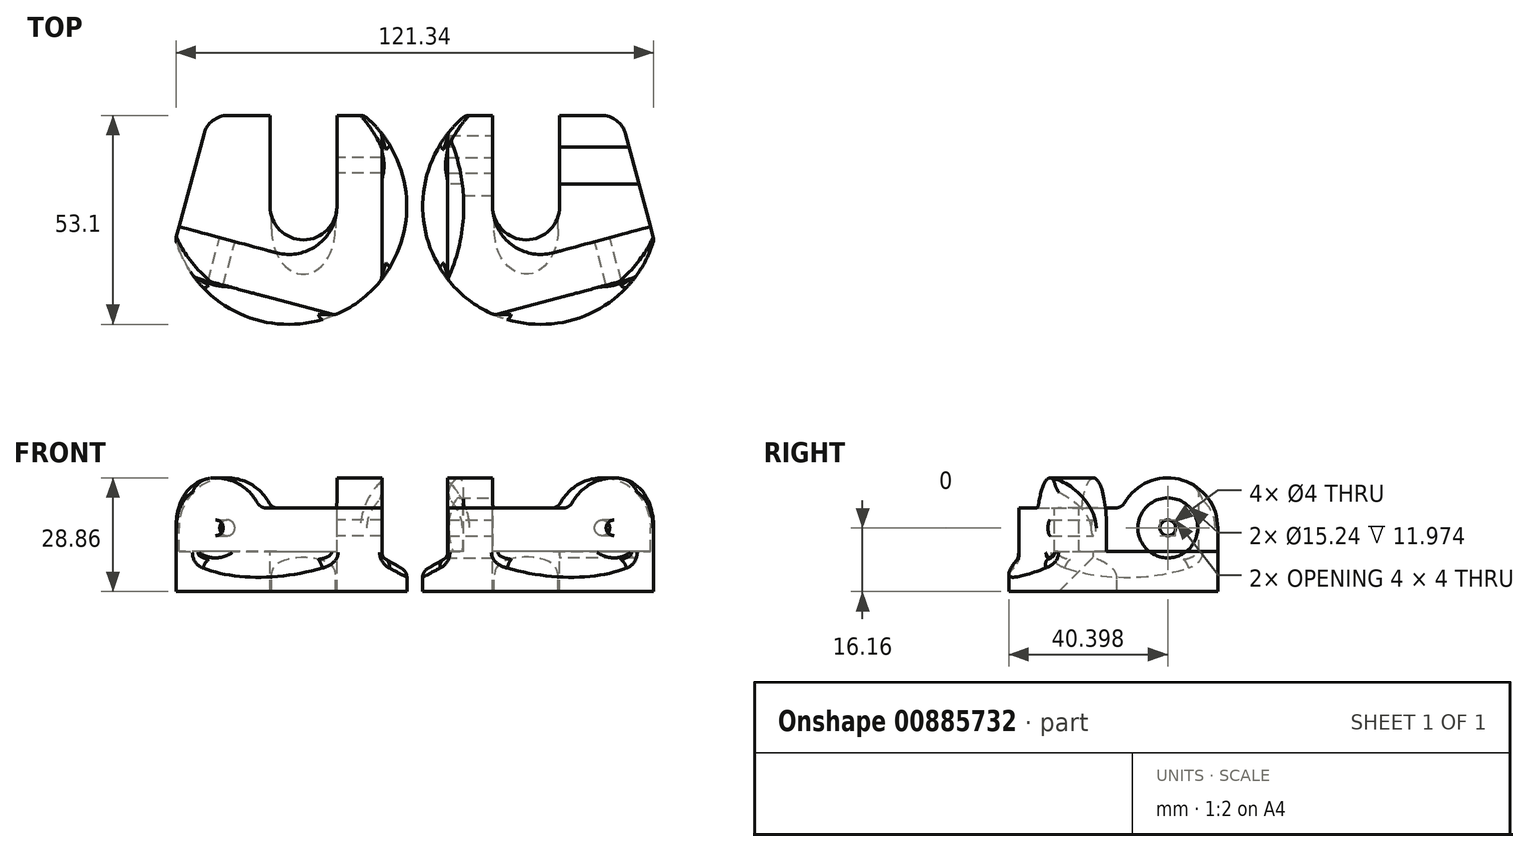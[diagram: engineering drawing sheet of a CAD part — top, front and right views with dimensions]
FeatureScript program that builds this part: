
annotation { "Feature Type Name" : "Feature", "Feature Type Description" : "" }
export const myFeature = defineFeature(function(context is Context, id is Id, definition is map)
    precondition{}
    {
        {
            var Q0;
            Q0=qCreatedBy(makeId("Top.planeOp"),FACE);
            var sketch = newSketch(context, id + "F0", { "sketchPlane" : qUnion([Q0])});
            skCircle(sketch, "E0", {"center": v(-32, 0) * mm, "radius": 30 * mm});
            skSolve(sketch);
        }
        {
            var Q0;
            Q0 = qSketchRegion(id + "F0", true);
            extrude(context, id + "F1", {"entities" : qUnion([Q0]), "depth" : 29 * mm, "offsetDistance" : 25.4 * mm});
        }
        {
            var Q0;
            Q0=makeQuery(id+"F1.opExtrude","CAP_FACE",FACE,{"disambiguationData":[OSD([sQuery(id+"F0.wireOp",EDGE,"E0")])],"isStart":false});
            var sketch = newSketch(context, id + "F2", { "sketchPlane" : qUnion([Q0])});
            skLineSegment(sketch, "E1", {"start": v(-61.63, -4.71) * mm, "end": v(-35.16, -11.8) * mm});
            skLineSegment(sketch, "E2", {"start": v(-19.78, 0) * mm, "end": v(-19.78, 27.4) * mm});
            skLineSegment(sketch, "E3", {"start": v(-8.35, -30.82) * mm, "end": v(-8.35, 27.4) * mm});
            skLineSegment(sketch, "E4", {"start": v(-8.35, -30.82) * mm, "end": v(-64.59, -15.75) * mm});
            skLineSegment(sketch, "E5", {"start": v(-64.59, -15.75) * mm, "end": v(-61.63, -4.71) * mm});
            skLineSegment(sketch, "E6", {"start": v(-19.78, 27.4) * mm, "end": v(-8.35, 27.4) * mm});
            skPoint(sketch, "E7.visualSharp", {"position": v(-19.78, -15.93) * mm});
            skArc(sketch, "E7.filletArc", {"start": v(-35.16, -11.8) * mm, "mid": v(-24.56, -9.7) * mm, "end": v(-19.78, 0) * mm});
            skCircle(sketch, "E8", {"center": v(-32, 0) * mm, "radius": 44.45 * mm});
            skSolve(sketch);
        }
        {
            var Q0;
            Q0 = qSketchRegion(id + "F2", true);
            var Q1;
            Q1=makeQuery(id+"F1.opExtrude","CAP_FACE",FACE,{"disambiguationData":[OSD([sQuery(id+"F0.wireOp",EDGE,"E0")])],"isStart":true});
            extrude(context, id + "F3", {"entities" : qUnion([Q0]), "operationType" : NewBodyOperationType.REMOVE, "endBound" : BoundingType.UP_TO_SURFACE, "oppositeDirection" : true, "depth" : 25.4 * mm, "endBoundEntityFace" : qUnion([Q1]), "hasOffset" : true, "offsetDistance" : 10.16 * mm});
        }
        {
            var Q0;
            {var subQ0=sQuery(id+"F2.wireOp",EDGE,"E1");var subQ1=sQuery(id+"F2.wireOp",EDGE,"E2");var subQ2=sQuery(id+"F2.wireOp",EDGE,"E7.filletArc");Q0=makeQuery(id+"F3.boolean.opBoolean","COPY",FACE,{"disambiguationData":[TD([makeQuery(id+"F3.opExtrude","SWEPT_FACE",FACE,{"disambiguationData":[OSD([subQ0])]})])],"derivedFrom":makeQuery(id+"F3.opExtrude","CAP_FACE",FACE,{"disambiguationData":[OSD([subQ0,subQ1,sQuery(id+"F2.wireOp",EDGE,"E3"),sQuery(id+"F2.wireOp",EDGE,"E4"),sQuery(id+"F2.wireOp",EDGE,"E5"),sQuery(id+"F2.wireOp",EDGE,"E6"),subQ2,sQuery(id+"F2.wireOp",EDGE,"E8")])],"isStart":false})});}
            var sketch = newSketch(context, id + "F4", { "sketchPlane" : qUnion([Q0])});
            skLineSegment(sketch, "E9.bottom", {"start": v(-19.78, 30) * mm, "end": v(-36.8, 30) * mm});
            skLineSegment(sketch, "E9.top", {"start": v(-19.78, 0) * mm, "end": v(-36.8, 0) * mm, "construction": true});
            skLineSegment(sketch, "E9.left", {"start": v(-19.78, 30) * mm, "end": v(-19.78, 0) * mm});
            skLineSegment(sketch, "E9.right", {"start": v(-36.8, 30) * mm, "end": v(-36.8, 0) * mm});
            skArc(sketch, "E10", {"start": v(-36.8, 0) * mm, "mid": v(-28.29, -8.5) * mm, "end": v(-19.78, 0) * mm});
            skSolve(sketch);
        }
        {
            var Q0;
            Q0 = qSketchRegion(id + "F4", true);
            extrude(context, id + "F5", {"entities" : qUnion([Q0]), "operationType" : NewBodyOperationType.REMOVE, "endBound" : BoundingType.THROUGH_ALL, "oppositeDirection" : true, "depth" : 25.4 * mm, "offsetDistance" : 25.4 * mm});
        }
        {
            var Q0;
            Q0=makeQuery(id+"F3.boolean.opBoolean","COPY",FACE,{"derivedFrom":makeQuery(id+"F3.opExtrude","SWEPT_FACE",FACE,{"disambiguationData":[OSD([sQuery(id+"F2.wireOp",EDGE,"E4")])]})});
            var sketch = newSketch(context, id + "F6", { "sketchPlane" : qUnion([Q0])});
            skPoint(sketch, "E11", {"position": v(-43.8, 16.16) * mm});
            skSolve(sketch);
        }
        {
            var Q0;
            Q0=makeQuery(id+"F3.boolean.opBoolean","COPY",FACE,{"derivedFrom":makeQuery(id+"F3.opExtrude","SWEPT_FACE",FACE,{"disambiguationData":[OSD([sQuery(id+"F2.wireOp",EDGE,"E3")])]})});
            var sketch = newSketch(context, id + "F7", { "sketchPlane" : qUnion([Q0])});
            skPoint(sketch, "E12", {"position": v(10.4, 16.16) * mm});
            skSolve(sketch);
        }
        {
            var Q0;
            Q0=sQuery(id+"F7.wireOp",VERTEX,"E12");
            var Q1;
            Q1=sQuery(id+"F6.wireOp",VERTEX,"E11");
            var Q2;
            Q2=makeQuery(id+"F1.opExtrude","SWEPT_BODY",BODY,{"disambiguationData":[OSD([sQuery(id+"F0.wireOp",EDGE,"E0")])]});
            hole(context, id + "F8", {"style" : HoleStyle.SIMPLE, "endStyle" : HoleEndStyle.THROUGH, "holeDiameter" : 4 * mm, "majorDiameter" : 6.35 * mm, "isTappedThrough" : true, "tappedDepth" : 12.7 * mm, "tapClearance" : 3, "locations" : qUnion([Q0, Q1]), "scope" : qUnion([Q2]), "startStyle" : HoleStartStyle.PART});
        }
        {
            var Q0;
            Q0=makeQuery(id+"F3.boolean.opBoolean","COPY",FACE,{"derivedFrom":makeQuery(id+"F3.opExtrude","SWEPT_FACE",FACE,{"disambiguationData":[OSD([sQuery(id+"F2.wireOp",EDGE,"E3")])]})});
            var sketch = newSketch(context, id + "F9", { "sketchPlane" : qUnion([Q0])});
            skCircle(sketch, "E13", {"center": v(10.4, 16.16) * mm, "radius": 7.62 * mm});
            skSolve(sketch);
        }
        {
            var Q0;
            Q0 = qSketchRegion(id + "F9", true);
            extrude(context, id + "F10", {"entities" : qUnion([Q0]), "operationType" : NewBodyOperationType.REMOVE, "endBound" : BoundingType.THROUGH_ALL, "depth" : 25.4 * mm, "offsetDistance" : 25.4 * mm});
        }
        {
            var Q0;
            Q0=makeQuery(id+"F3.boolean.opBoolean","COPY",FACE,{"derivedFrom":makeQuery(id+"F3.opExtrude","SWEPT_FACE",FACE,{"disambiguationData":[OSD([sQuery(id+"F2.wireOp",EDGE,"E4")])]})});
            var sketch = newSketch(context, id + "F11", { "sketchPlane" : qUnion([Q0])});
            skCircle(sketch, "E14", {"center": v(-43.8, 16.16) * mm, "radius": 7.62 * mm});
            skSolve(sketch);
        }
        {
            var Q0;
            Q0 = qSketchRegion(id + "F11", true);
            extrude(context, id + "F12", {"entities" : qUnion([Q0]), "operationType" : NewBodyOperationType.REMOVE, "endBound" : BoundingType.THROUGH_ALL, "depth" : 25.4 * mm, "offsetDistance" : 25.4 * mm});
        }
        {
            var Q0;
            {var subQ0=sQuery(id+"F2.wireOp",EDGE,"E3");Q0=makeQuery(id+"F10.boolean.opBoolean","INTERSECT",EDGE,{"disambiguationData":[OD(1.0)],"derivedFrom":[makeQuery(id+"F3.boolean.opBoolean","COPY",FACE,{"disambiguationData":[TD([makeQuery(id+"F3.opExtrude","SWEPT_FACE",FACE,{"disambiguationData":[OSD([subQ0])]})])],"derivedFrom":makeQuery(id+"F3.opExtrude","CAP_FACE",FACE,{"disambiguationData":[OSD([sQuery(id+"F2.wireOp",EDGE,"E1"),sQuery(id+"F2.wireOp",EDGE,"E2"),subQ0,sQuery(id+"F2.wireOp",EDGE,"E4"),sQuery(id+"F2.wireOp",EDGE,"E5"),sQuery(id+"F2.wireOp",EDGE,"E6"),sQuery(id+"F2.wireOp",EDGE,"E7.filletArc"),sQuery(id+"F2.wireOp",EDGE,"E8")])],"isStart":false})}),makeQuery(id+"F10.opExtrude","SWEPT_FACE",FACE,{"disambiguationData":[OSD([sQuery(id+"F9.wireOp",EDGE,"E13")])]})]});}
            cPlane(context, id + "F13", {"entities" : qUnion([Q0]), "cplaneType" : CPlaneType.LINE_ANGLE, "offset" : 25.4 * mm, "angle" : 45 * degree, "oppositeDirection" : true, "width" : 152.4 * mm, "height" : 152.4 * mm});
        }
        {
            var Q0;
            Q0=qCreatedBy(id+"F13.planeOp",FACE);
            var sketch = newSketch(context, id + "F14", { "sketchPlane" : qUnion([Q0])});
            skLineSegment(sketch, "E15.0", {"start": v(-19.78, 2.07) * mm, "end": v(-19.78, 6.07) * mm, "construction": true});
            skLineSegment(sketch, "E16", {"start": v(-19.78, 4.07) * mm, "end": v(-36.8, 4.07) * mm, "construction": true});
            skLineSegment(sketch, "E17", {"start": v(-36.8, 4.07) * mm, "end": v(-36.8, 0) * mm, "construction": true});
            skArc(sketch, "E18", {"start": v(-20.16, 4.07) * mm, "mid": v(-28.29, 12.2) * mm, "end": v(-36.42, 4.07) * mm});
            skLineSegment(sketch, "E19", {"start": v(-36.42, 4.07) * mm, "end": v(-36.42, 0) * mm});
            skLineSegment(sketch, "E20", {"start": v(-36.42, 0) * mm, "end": v(-20.16, 0) * mm});
            skLineSegment(sketch, "E21", {"start": v(-20.16, 0) * mm, "end": v(-20.16, 4.07) * mm});
            skSolve(sketch);
        }
        {
            var Q0;
            Q0=makeQuery(id+"F14.imprint","IMPRINT",FACE,{"disambiguationData":[TD([[makeQuery(id+"F14.imprint","IMPRINT",EDGE,{"derivedFrom":sQuery(id+"F14.wireOp",EDGE,"E18")}),1.0]])]});
            extrude(context, id + "F15", {"entities" : qUnion([Q0]), "operationType" : NewBodyOperationType.REMOVE, "endBound" : BoundingType.THROUGH_ALL, "depth" : 25.4 * mm, "offsetDistance" : 25.4 * mm});
        }
        {
            var Q0;
            Q0=makeQuery(id+"F10.boolean.opBoolean","MERGE",FACE,{"derivedFrom":[makeQuery(id+"F3.boolean.opBoolean","COPY",FACE,{"derivedFrom":makeQuery(id+"F3.opExtrude","SWEPT_FACE",FACE,{"disambiguationData":[OSD([sQuery(id+"F2.wireOp",EDGE,"E3")])]})})],"fromTools":[makeQuery(id+"F10.opExtrude","CAP_FACE",FACE,{"disambiguationData":[OSD([sQuery(id+"F9.wireOp",EDGE,"E13")])],"isStart":true})]});
            var sketch = newSketch(context, id + "F16", { "sketchPlane" : qUnion([Q0])});
            skArc(sketch, "E22", {"start": v(23.1, 16.16) * mm, "mid": v(13, 28.6) * mm, "end": v(-1.24, 21.24) * mm});
            skLineSegment(sketch, "E23", {"start": v(-1.24, 21.24) * mm, "end": v(-40.4, 21.24) * mm});
            skLineSegment(sketch, "E24", {"start": v(-40.4, 21.24) * mm, "end": v(-40.4, 30.13) * mm});
            skLineSegment(sketch, "E25", {"start": v(-40.4, 30.13) * mm, "end": v(35.8, 30.13) * mm});
            skLineSegment(sketch, "E26", {"start": v(35.8, 30.13) * mm, "end": v(35.8, 0) * mm});
            skLineSegment(sketch, "E27", {"start": v(35.8, 0) * mm, "end": v(23.1, 0) * mm});
            skLineSegment(sketch, "E28", {"start": v(23.1, 0) * mm, "end": v(23.1, 16.16) * mm});
            skSolve(sketch);
        }
        {
            var Q0;
            Q0 = qSketchRegion(id + "F16", true);
            extrude(context, id + "F17", {"entities" : qUnion([Q0]), "operationType" : NewBodyOperationType.REMOVE, "oppositeDirection" : true, "depth" : 20.32 * mm, "offsetDistance" : 25.4 * mm});
        }
        {
            var Q0;
            Q0=makeQuery(id+"F12.boolean.opBoolean","MERGE",FACE,{"derivedFrom":[makeQuery(id+"F3.boolean.opBoolean","COPY",FACE,{"derivedFrom":makeQuery(id+"F3.opExtrude","SWEPT_FACE",FACE,{"disambiguationData":[OSD([sQuery(id+"F2.wireOp",EDGE,"E4")])]})})],"fromTools":[makeQuery(id+"F12.opExtrude","CAP_FACE",FACE,{"disambiguationData":[OSD([sQuery(id+"F11.wireOp",EDGE,"E14")])],"isStart":true})]});
            var sketch = newSketch(context, id + "F18", { "sketchPlane" : qUnion([Q0])});
            skArc(sketch, "E29", {"start": v(-32.17, 21.24) * mm, "mid": v(-46.4, 28.6) * mm, "end": v(-56.5, 16.16) * mm});
            skLineSegment(sketch, "E30", {"start": v(-32.17, 21.24) * mm, "end": v(0, 21.24) * mm});
            skLineSegment(sketch, "E31", {"start": v(0, 21.24) * mm, "end": v(0, 32.5) * mm});
            skLineSegment(sketch, "E32", {"start": v(0, 32.5) * mm, "end": v(-68.24, 32.5) * mm});
            skLineSegment(sketch, "E33", {"start": v(-68.24, 32.5) * mm, "end": v(-68.24, -6.41) * mm});
            skLineSegment(sketch, "E34", {"start": v(-68.24, -6.41) * mm, "end": v(-56.5, -6.41) * mm});
            skLineSegment(sketch, "E35", {"start": v(-56.5, -6.41) * mm, "end": v(-56.5, 16.16) * mm});
            skSolve(sketch);
        }
        {
            var Q0;
            Q0 = qSketchRegion(id + "F18", true);
            extrude(context, id + "F19", {"entities" : qUnion([Q0]), "operationType" : NewBodyOperationType.REMOVE, "oppositeDirection" : true, "depth" : 20.32 * mm, "offsetDistance" : 25.4 * mm});
        }
        {
            var Q0;
            {var subQ0=sQuery(id+"F2.wireOp",EDGE,"E1");var subQ1=sQuery(id+"F2.wireOp",EDGE,"E2");var subQ2=sQuery(id+"F2.wireOp",EDGE,"E7.filletArc");Q0=makeQuery(id+"F3.boolean.opBoolean","COPY",FACE,{"disambiguationData":[TD([makeQuery(id+"F3.opExtrude","SWEPT_FACE",FACE,{"disambiguationData":[OSD([subQ0])]})])],"derivedFrom":makeQuery(id+"F3.opExtrude","CAP_FACE",FACE,{"disambiguationData":[OSD([subQ0,subQ1,sQuery(id+"F2.wireOp",EDGE,"E3"),sQuery(id+"F2.wireOp",EDGE,"E4"),sQuery(id+"F2.wireOp",EDGE,"E5"),sQuery(id+"F2.wireOp",EDGE,"E6"),subQ2,sQuery(id+"F2.wireOp",EDGE,"E8")])],"isStart":false})});}
            var sketch = newSketch(context, id + "F20", { "sketchPlane" : qUnion([Q0])});
            skArc(sketch, "E36.0", {"start": v(-36.8, 29.61) * mm, "mid": v(-53.32, 21.1) * mm, "end": v(-61.66, 4.5) * mm});
            skLineSegment(sketch, "E36.1", {"start": v(-61.66, 4.5) * mm, "end": v(-57.59, 3.4) * mm});
            skLineSegment(sketch, "E36.3", {"start": v(-36.8, 29.61) * mm, "end": v(-36.8, 23.1) * mm});
            skLineSegment(sketch, "E37", {"start": v(-57.59, 3.4) * mm, "end": v(-53.57, 18.4) * mm});
            skLineSegment(sketch, "E38", {"start": v(-47.44, 23.1) * mm, "end": v(-36.8, 23.1) * mm});
            skPoint(sketch, "E39.orphan", {"position": v(-36.8, 0) * mm});
            skPoint(sketch, "E40.visualSharp", {"position": v(-52.31, 23.1) * mm});
            skArc(sketch, "E40.filletArc", {"start": v(-47.44, 23.1) * mm, "mid": v(-51.3, 21.79) * mm, "end": v(-53.57, 18.4) * mm});
            skSolve(sketch);
        }
        {
            var Q0;
            Q0=makeQuery(id+"F20.imprint","IMPRINT",FACE,{"disambiguationData":[TD([[makeQuery(id+"F20.imprint","IMPRINT",EDGE,{"derivedFrom":sQuery(id+"F20.wireOp",EDGE,"E36.0")}),1.0]])]});
            extrude(context, id + "F21", {"entities" : qUnion([Q0]), "operationType" : NewBodyOperationType.REMOVE, "oppositeDirection" : true, "depth" : 25.4 * mm, "offsetDistance" : 25.4 * mm});
        }
        {
            var Q0;
            Q0=makeQuery(id+"F17.boolean.opBoolean","COPY",FACE,{"derivedFrom":makeQuery(id+"F17.opExtrude","SWEPT_FACE",FACE,{"disambiguationData":[OSD([sQuery(id+"F16.wireOp",EDGE,"E28")])]})});
            var sketch = newSketch(context, id + "F22", { "sketchPlane" : qUnion([Q0])});
            skLineSegment(sketch, "E41", {"start": v(2, 5.08) * mm, "end": v(7.33, 8.16) * mm});
            skLineSegment(sketch, "E42", {"start": v(8.35, 9.92) * mm, "end": v(8.35, 17.78) * mm});
            skLineSegment(sketch, "E43", {"start": v(8.35, 17.78) * mm, "end": v(2, 17.78) * mm});
            skLineSegment(sketch, "E44", {"start": v(2, 17.78) * mm, "end": v(2, 5.08) * mm});
            skPoint(sketch, "E45.visualSharp", {"position": v(8.35, 8.75) * mm});
            skArc(sketch, "E45.filletArc", {"start": v(7.33, 8.16) * mm, "mid": v(8.08, 8.9) * mm, "end": v(8.35, 9.92) * mm});
            skLineSegment(sketch, "E46.0", {"start": v(60.78, 0) * mm, "end": v(2, 0) * mm});
            skSolve(sketch);
        }
        {
            var Q0;
            Q0 = qSketchRegion(id + "F22", true);
            extrude(context, id + "F23", {"entities" : qUnion([Q0]), "operationType" : NewBodyOperationType.REMOVE, "endBound" : BoundingType.THROUGH_ALL, "oppositeDirection" : true, "depth" : 25.4 * mm, "offsetDistance" : 25.4 * mm});
        }
        {
            var Q0;
            Q0=makeQuery(id+"F21.boolean.opBoolean","MERGE",FACE,{"derivedFrom":[makeQuery(id+"F19.boolean.opBoolean","COPY",FACE,{"derivedFrom":makeQuery(id+"F19.opExtrude","SWEPT_FACE",FACE,{"disambiguationData":[OSD([sQuery(id+"F18.wireOp",EDGE,"E35")])]})})],"fromTools":[makeQuery(id+"F21.opExtrude","SWEPT_FACE",FACE,{"disambiguationData":[OSD([sQuery(id+"F20.wireOp",EDGE,"E37")])]})]});
            var sketch = newSketch(context, id + "F24", { "sketchPlane" : qUnion([Q0])});
            skLineSegment(sketch, "E47", {"start": v(31.93, 17.78) * mm, "end": v(38.28, 17.78) * mm});
            skLineSegment(sketch, "E48", {"start": v(38.28, 17.78) * mm, "end": v(38.28, 5.08) * mm});
            skLineSegment(sketch, "E49", {"start": v(38.28, 5.08) * mm, "end": v(32.95, 8.16) * mm});
            skLineSegment(sketch, "E50", {"start": v(31.93, 9.92) * mm, "end": v(31.93, 17.78) * mm});
            skPoint(sketch, "E51.visualSharp", {"position": v(31.93, 8.75) * mm});
            skArc(sketch, "E51.filletArc", {"start": v(31.93, 9.92) * mm, "mid": v(32.2, 8.9) * mm, "end": v(32.95, 8.16) * mm});
            skLineSegment(sketch, "E52.0", {"start": v(38.28, 0) * mm, "end": v(-18.98, 0) * mm, "construction": true});
            skSolve(sketch);
        }
        {
            var Q0;
            Q0 = qSketchRegion(id + "F24", true);
            extrude(context, id + "F25", {"entities" : qUnion([Q0]), "operationType" : NewBodyOperationType.REMOVE, "endBound" : BoundingType.THROUGH_ALL, "oppositeDirection" : true, "depth" : 25.4 * mm, "offsetDistance" : 25.4 * mm});
        }
        {
            var Q0;
            Q0=makeQuery(id+"F19.boolean.opBoolean","INTERSECT",EDGE,{"derivedFrom":[makeQuery(id+"F1.opExtrude","SWEPT_FACE",FACE,{"disambiguationData":[OSD([sQuery(id+"F0.wireOp",EDGE,"E0")])]}),makeQuery(id+"F19.opExtrude","SWEPT_FACE",FACE,{"disambiguationData":[OSD([sQuery(id+"F18.wireOp",EDGE,"E35")])]})]});
            var Q1;
            Q1=makeQuery(id+"F17.boolean.opBoolean","INTERSECT",EDGE,{"derivedFrom":[makeQuery(id+"F1.opExtrude","SWEPT_FACE",FACE,{"disambiguationData":[OSD([sQuery(id+"F0.wireOp",EDGE,"E0")])]}),makeQuery(id+"F17.opExtrude","SWEPT_FACE",FACE,{"disambiguationData":[OSD([sQuery(id+"F16.wireOp",EDGE,"E28")])]})]});
            var Q2;
            {var subQ0=sQuery(id+"F0.wireOp",EDGE,"E0");var subQ1=makeQuery(id+"F1.opExtrude","SWEPT_FACE",FACE,{"disambiguationData":[OSD([subQ0])]});var subQ4=sQuery(id+"F2.wireOp",EDGE,"E3");var subQ6=makeQuery(id+"F3.opExtrude","SWEPT_FACE",FACE,{"disambiguationData":[OSD([subQ4])]});Q2=makeQuery(id+"F25.boolean.opBoolean","INTERSECT",EDGE,{"disambiguationData":[OD(0.0)],"derivedFrom":[makeQuery(id+"F19.boolean.opBoolean","SPLIT",FACE,{"disambiguationData":[TD([makeQuery(id+"F3.boolean.opBoolean","COPY",FACE,{"derivedFrom":subQ6})])],"derivedFrom":subQ1}),makeQuery(id+"F25.opExtrude","SWEPT_FACE",FACE,{"disambiguationData":[OSD([sQuery(id+"F24.wireOp",EDGE,"E50")])]})]});}
            var Q3;
            {var subQ0=sQuery(id+"F0.wireOp",EDGE,"E0");var subQ1=makeQuery(id+"F1.opExtrude","SWEPT_FACE",FACE,{"disambiguationData":[OSD([subQ0])]});var subQ4=sQuery(id+"F2.wireOp",EDGE,"E3");var subQ6=makeQuery(id+"F3.opExtrude","SWEPT_FACE",FACE,{"disambiguationData":[OSD([subQ4])]});Q3=makeQuery(id+"F23.boolean.opBoolean","INTERSECT",EDGE,{"disambiguationData":[OD(1.0)],"derivedFrom":[makeQuery(id+"F19.boolean.opBoolean","SPLIT",FACE,{"disambiguationData":[TD([makeQuery(id+"F3.boolean.opBoolean","COPY",FACE,{"derivedFrom":subQ6})])],"derivedFrom":subQ1}),makeQuery(id+"F23.opExtrude","SWEPT_FACE",FACE,{"disambiguationData":[OSD([sQuery(id+"F22.wireOp",EDGE,"E42")])]})]});}
            var Q4;
            Q4=makeQuery(id+"F17.boolean.opBoolean","COPY",EDGE,{"derivedFrom":makeQuery(id+"F17.opExtrude","SWEPT_EDGE",EDGE,{"disambiguationData":[OSD([sQuery(id+"F16.wireOp",EDGE,"E22"),sQuery(id+"F16.wireOp",EDGE,"E23")])]})});
            var Q5;
            Q5=makeQuery(id+"F19.boolean.opBoolean","COPY",EDGE,{"derivedFrom":makeQuery(id+"F19.opExtrude","SWEPT_EDGE",EDGE,{"disambiguationData":[OSD([sQuery(id+"F18.wireOp",EDGE,"E29"),sQuery(id+"F18.wireOp",EDGE,"E30")])]})});
            var Q6;
            Q6=makeQuery(id+"F17.boolean.opBoolean","COPY",EDGE,{"derivedFrom":makeQuery(id+"F17.opExtrude","CAP_EDGE",EDGE,{"disambiguationData":[OSD([sQuery(id+"F16.wireOp",EDGE,"E23")])],"isStart":true})});
            var Q7;
            Q7=makeQuery(id+"F17.boolean.opBoolean","INTERSECT",EDGE,{"derivedFrom":[makeQuery(id+"F1.opExtrude","SWEPT_FACE",FACE,{"disambiguationData":[OSD([sQuery(id+"F0.wireOp",EDGE,"E0")])]}),makeQuery(id+"F17.opExtrude","SWEPT_FACE",FACE,{"disambiguationData":[OSD([sQuery(id+"F16.wireOp",EDGE,"E23")])]})]});
            var Q8;
            Q8=makeQuery(id+"F19.boolean.opBoolean","MERGE",EDGE,{"derivedFrom":[makeQuery(id+"F17.boolean.opBoolean","INTERSECT",EDGE,{"derivedFrom":[makeQuery(id+"F12.boolean.opBoolean","MERGE",FACE,{"derivedFrom":[makeQuery(id+"F3.boolean.opBoolean","COPY",FACE,{"derivedFrom":makeQuery(id+"F3.opExtrude","SWEPT_FACE",FACE,{"disambiguationData":[OSD([sQuery(id+"F2.wireOp",EDGE,"E4")])]})})],"fromTools":[makeQuery(id+"F12.opExtrude","CAP_FACE",FACE,{"disambiguationData":[OSD([sQuery(id+"F11.wireOp",EDGE,"E14")])],"isStart":true})]}),makeQuery(id+"F17.opExtrude","SWEPT_FACE",FACE,{"disambiguationData":[OSD([sQuery(id+"F16.wireOp",EDGE,"E23")])]})]})],"fromTools":[makeQuery(id+"F19.opExtrude","CAP_EDGE",EDGE,{"disambiguationData":[OSD([sQuery(id+"F18.wireOp",EDGE,"E30")])],"isStart":true})]});
            fillet(context, id + "F26", {"entities" : qUnion([Q0, Q1, Q2, Q3, Q4, Q5, Q6, Q7, Q8]), "radius" : 2.54 * mm, "tangentPropagation" : true, "allowEdgeOverflow" : false});
        }
        {
            var Q0;
            Q0=makeQuery(id+"F1.opExtrude","SWEPT_BODY",BODY,{"disambiguationData":[OSD([sQuery(id+"F0.wireOp",EDGE,"E0")])]});
            var Q1;
            Q1=qCreatedBy(makeId("Right.planeOp"),FACE);
            mirror(context, id + "F27", {"entities" : qUnion([Q0]), "mirrorPlane" : qUnion([Q1])});
        }
    });
